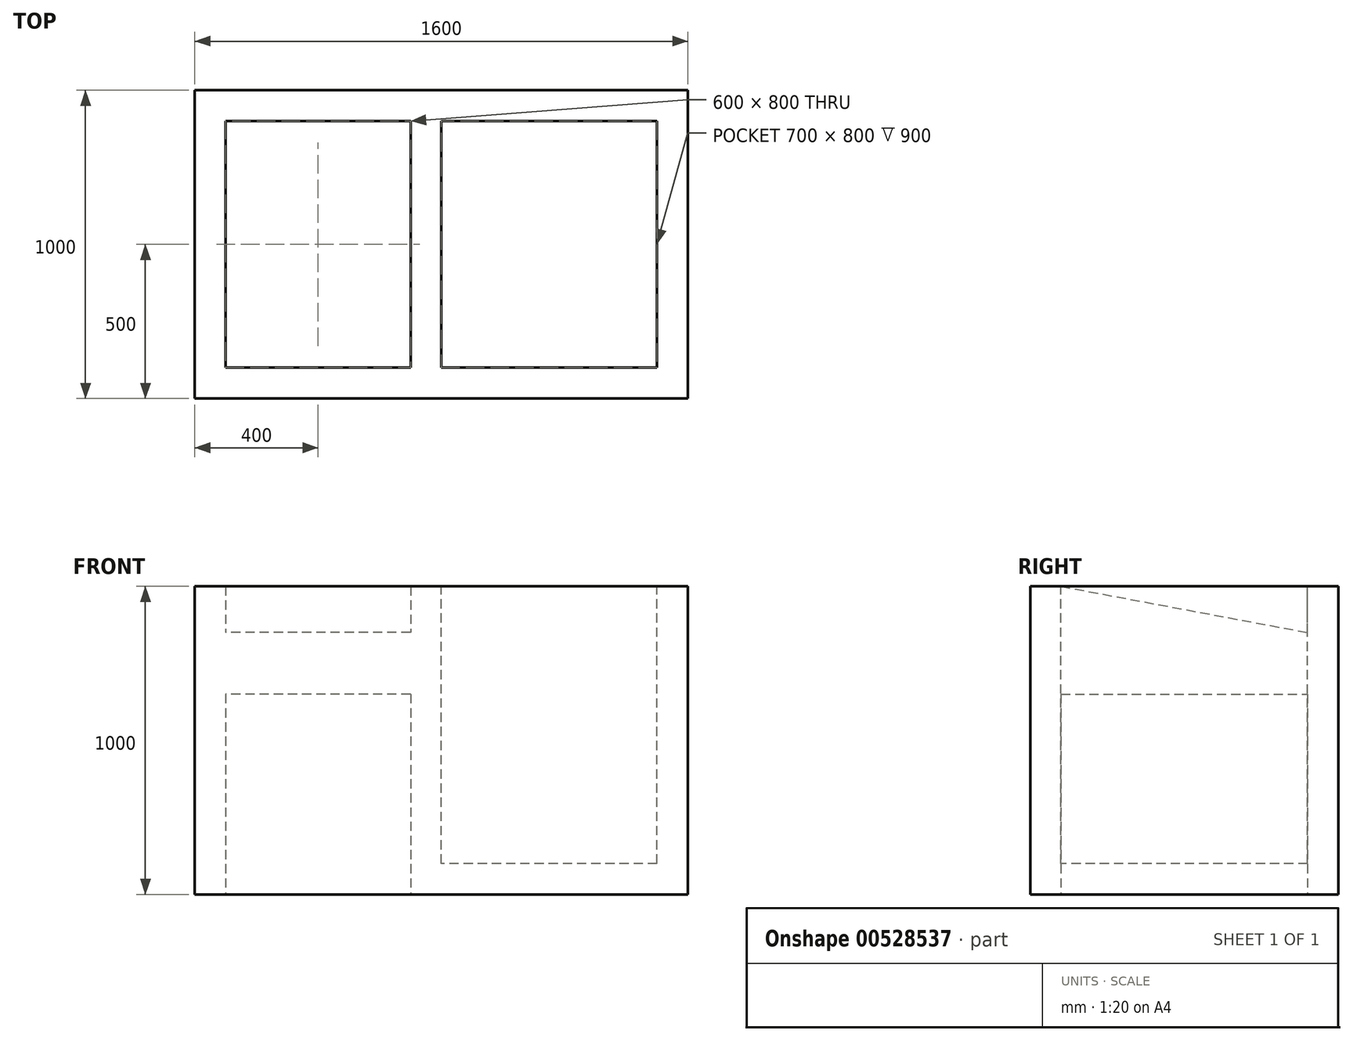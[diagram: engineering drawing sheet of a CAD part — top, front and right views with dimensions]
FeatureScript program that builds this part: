
annotation { "Feature Type Name" : "Feature", "Feature Type Description" : "" }
export const myFeature = defineFeature(function(context is Context, id is Id, definition is map)
    precondition{}
    {
        {
            var Q0;
            Q0=qCreatedBy(makeId("Top.planeOp"),FACE);
            var sketch = newSketch(context, id + "F0", { "sketchPlane" : qUnion([Q0])});
            skLineSegment(sketch, "E0.bottom", {"start": v(800, -500) * mm, "end": v(-800, -500) * mm});
            skLineSegment(sketch, "E0.top", {"start": v(800, 500) * mm, "end": v(-800, 500) * mm});
            skLineSegment(sketch, "E0.left", {"start": v(800, -500) * mm, "end": v(800, 500) * mm});
            skLineSegment(sketch, "E0.right", {"start": v(-800, -500) * mm, "end": v(-800, 500) * mm});
            skPoint(sketch, "E0.middle", {"position": v(0, 0) * mm});
            skSolve(sketch);
        }
        {
            var Q0;
            Q0=makeQuery(id+"F0.imprint","IMPRINT",FACE,{"disambiguationData":[TD([[makeQuery(id+"F0.imprint","IMPRINT",EDGE,{"derivedFrom":sQuery(id+"F0.wireOp",EDGE,"E0.bottom")}),-1.0]])]});
            extrude(context, id + "F1", {"entities" : qUnion([Q0]), "depth" : 1000 * mm, "offsetDistance" : 25 * mm});
        }
        {
            var Q0;
            Q0=makeQuery(id+"F1.opExtrude","CAP_FACE",FACE,{"disambiguationData":[OSD([sQuery(id+"F0.wireOp",EDGE,"E0.bottom"),sQuery(id+"F0.wireOp",EDGE,"E0.top"),sQuery(id+"F0.wireOp",EDGE,"E0.left"),sQuery(id+"F0.wireOp",EDGE,"E0.right")])],"isStart":false});
            var sketch = newSketch(context, id + "F2", { "sketchPlane" : qUnion([Q0])});
            skLineSegment(sketch, "E1.bottom", {"start": v(700, 400) * mm, "end": v(0, 400) * mm});
            skLineSegment(sketch, "E1.top", {"start": v(700, -400) * mm, "end": v(0, -400) * mm});
            skLineSegment(sketch, "E1.left", {"start": v(700, 400) * mm, "end": v(700, -400) * mm});
            skLineSegment(sketch, "E1.right", {"start": v(0, 400) * mm, "end": v(0, -400) * mm});
            skSolve(sketch);
        }
        {
            var Q0;
            Q0=qSketchRegion(id+"F2",true);
            extrude(context, id + "F3", {"entities" : qUnion([Q0]), "operationType" : NewBodyOperationType.REMOVE, "oppositeDirection" : true, "depth" : 900 * mm, "offsetDistance" : 25 * mm});
        }
        {
            var Q0;
            Q0=makeQuery(id+"F1.opExtrude","SWEPT_FACE",FACE,{"disambiguationData":[OSD([sQuery(id+"F0.wireOp",EDGE,"E0.right")])]});
            cPlane(context, id + "F4", {"entities" : qUnion([Q0]), "cplaneType" : CPlaneType.OFFSET, "offset" : 100 * mm, "oppositeDirection" : true, "width" : 150 * mm, "height" : 150 * mm});
        }
        {
            var Q0;
            Q0=qCreatedBy(id+"F4.planeOp",FACE);
            var sketch = newSketch(context, id + "F5", { "sketchPlane" : qUnion([Q0])});
            skLineSegment(sketch, "E2.0", {"start": v(400, 1000) * mm, "end": v(-400, 1000) * mm});
            skLineSegment(sketch, "E3", {"start": v(400, 1000) * mm, "end": v(-400, 850) * mm});
            skLineSegment(sketch, "E4", {"start": v(-400, 850) * mm, "end": v(-400, 1000) * mm});
            skPoint(sketch, "E5.orphan", {"position": v(-500, 1000) * mm});
            skPoint(sketch, "E6.orphan", {"position": v(500, 1000) * mm});
            skSolve(sketch);
        }
        {
            var Q0;
            Q0=qCreatedBy(makeId("Right.planeOp"),FACE);
            cPlane(context, id + "F6", {"entities" : qUnion([Q0]), "cplaneType" : CPlaneType.OFFSET, "offset" : 100 * mm, "oppositeDirection" : true, "width" : 150 * mm, "height" : 150 * mm});
        }
        {
            var Q0;
            Q0=qSketchRegion(id+"F5",true);
            var Q1;
            Q1=qCreatedBy(id+"F6.planeOp",FACE);
            extrude(context, id + "F7", {"entities" : qUnion([Q0]), "operationType" : NewBodyOperationType.REMOVE, "endBound" : BoundingType.UP_TO_SURFACE, "oppositeDirection" : true, "depth" : 25 * mm, "endBoundEntityFace" : qUnion([Q1]), "offsetDistance" : 25 * mm});
        }
        {
            var Q0;
            Q0=makeQuery(id+"F1.opExtrude","CAP_FACE",FACE,{"disambiguationData":[OSD([sQuery(id+"F0.wireOp",EDGE,"E0.bottom"),sQuery(id+"F0.wireOp",EDGE,"E0.top"),sQuery(id+"F0.wireOp",EDGE,"E0.left"),sQuery(id+"F0.wireOp",EDGE,"E0.right")])],"isStart":true});
            var sketch = newSketch(context, id + "F8", { "sketchPlane" : qUnion([Q0])});
            skLineSegment(sketch, "E7.0", {"start": v(-100, 400) * mm, "end": v(-700, 400) * mm});
            skLineSegment(sketch, "E8.0", {"start": v(-100, 400) * mm, "end": v(-100, -400) * mm});
            skLineSegment(sketch, "E9.0", {"start": v(-100, -400) * mm, "end": v(-700, -400) * mm});
            skLineSegment(sketch, "E10.0", {"start": v(-700, 400) * mm, "end": v(-700, -400) * mm});
            skSolve(sketch);
        }
        {
            var Q0;
            Q0=qSketchRegion(id+"F8",true);
            extrude(context, id + "F9", {"entities" : qUnion([Q0]), "operationType" : NewBodyOperationType.REMOVE, "oppositeDirection" : true, "depth" : 650 * mm, "offsetDistance" : 25 * mm});
        }
    });
